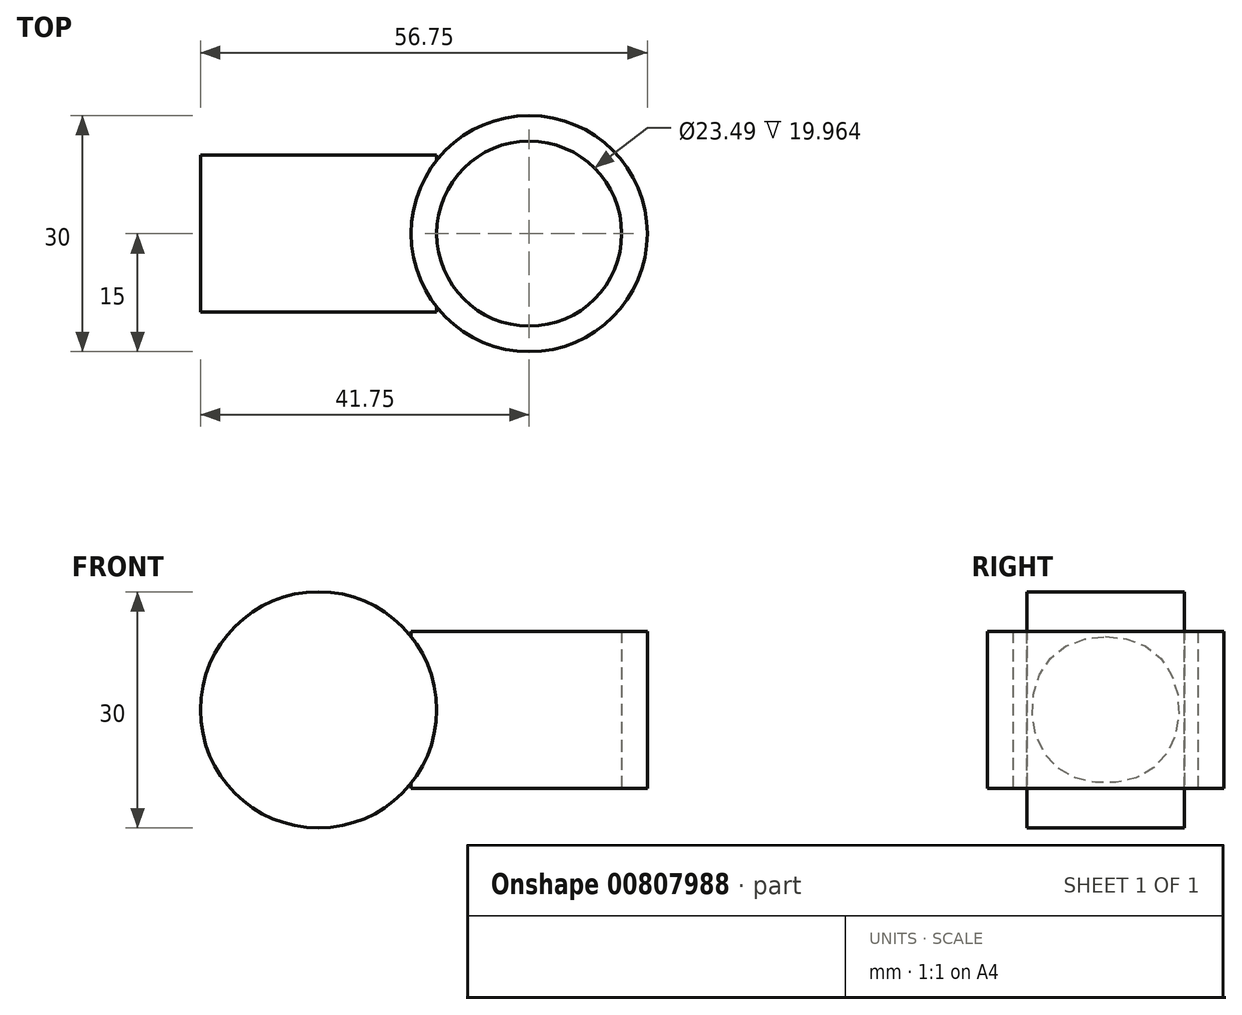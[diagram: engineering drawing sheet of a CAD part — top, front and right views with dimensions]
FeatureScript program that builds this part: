
annotation { "Feature Type Name" : "Feature", "Feature Type Description" : "" }
export const myFeature = defineFeature(function(context is Context, id is Id, definition is map)
    precondition{}
    {
        {
            var Q0;
            Q0=qCreatedBy(makeId("Top.planeOp"),FACE);
            var sketch = newSketch(context, id + "F0", { "sketchPlane" : qUnion([Q0])});
            skCircle(sketch, "E0", {"center": v(0, 0) * mm, "radius": 11.75 * mm});
            skCircle(sketch, "E1", {"center": v(0, 0) * mm, "radius": 15 * mm});
            skSolve(sketch);
        }
        {
            var Q0;
            Q0 = qSketchRegion(id + "F0", true);
            extrude(context, id + "F1", {"entities" : qUnion([Q0]), "depth" : 9.98 * mm, "offsetDistance" : 25.4 * mm, "hasSecondDirection" : true, "secondDirectionOppositeDirection" : true, "secondDirectionDepth" : 9.98 * mm});
        }
        {
            var Q0;
            Q0=qCreatedBy(makeId("Front.planeOp"),FACE);
            var sketch = newSketch(context, id + "F2", { "sketchPlane" : qUnion([Q0])});
            skCircle(sketch, "E2", {"center": v(-26.75, 0) * mm, "radius": 11.75 * mm});
            skCircle(sketch, "E3", {"center": v(-26.75, 0) * mm, "radius": 15 * mm});
            skSolve(sketch);
        }
        {
            var Q0;
            Q0=makeQuery(id+"F2.imprint","IMPRINT",FACE,{"disambiguationData":[TD([[makeQuery(id+"F2.imprint","IMPRINT",EDGE,{"derivedFrom":sQuery(id+"F2.wireOp",EDGE,"E2")}),-1.0]])]});
            var Q1;
            Q1=makeQuery(id+"F2.imprint","IMPRINT",FACE,{"disambiguationData":[TD([[makeQuery(id+"F2.imprint","IMPRINT",EDGE,{"derivedFrom":sQuery(id+"F2.wireOp",EDGE,"E2")}),1.0]])]});
            extrude(context, id + "F3", {"entities" : qUnion([Q0, Q1]), "operationType" : NewBodyOperationType.ADD, "depth" : 9.98 * mm, "offsetDistance" : 25.4 * mm, "hasSecondDirection" : true, "secondDirectionOppositeDirection" : true, "secondDirectionDepth" : 9.98 * mm});
        }
    });
